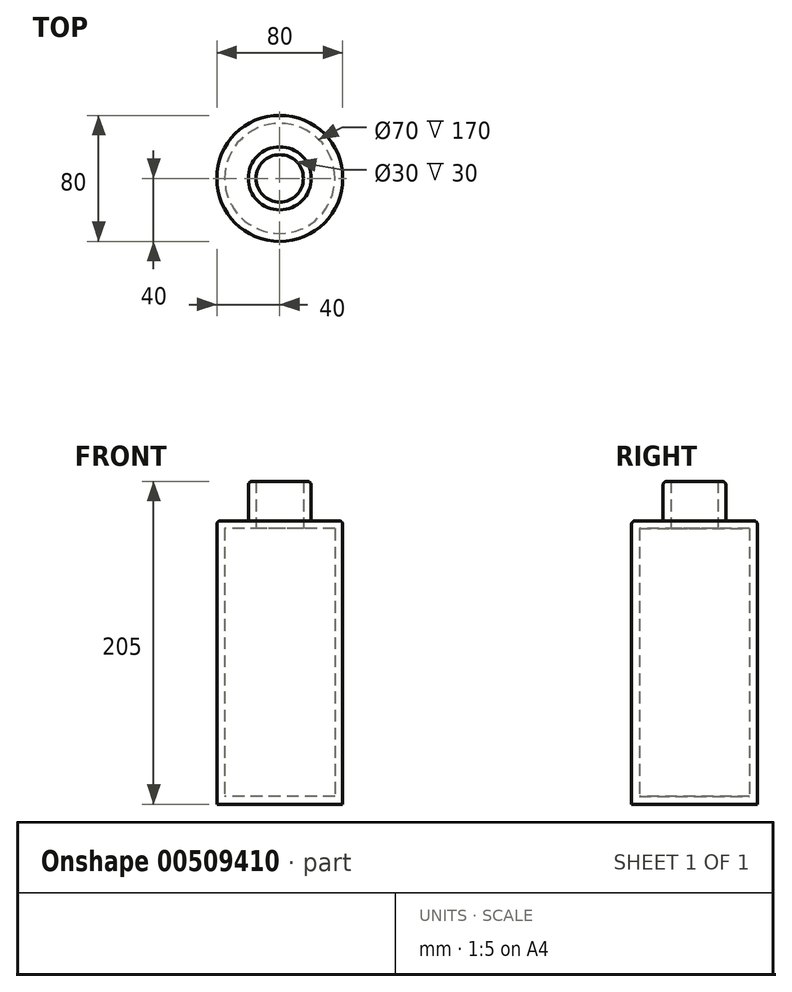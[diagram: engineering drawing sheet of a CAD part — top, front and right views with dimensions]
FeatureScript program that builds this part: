
annotation { "Feature Type Name" : "Feature", "Feature Type Description" : "" }
export const myFeature = defineFeature(function(context is Context, id is Id, definition is map)
    precondition{}
    {
        {
            var Q0;
            Q0=qCreatedBy(makeId("Top.planeOp"),FACE);
            var sketch = newSketch(context, id + "F0", { "sketchPlane" : qUnion([Q0])});
            skCircle(sketch, "E0", {"center": v(0, 0) * mm, "radius": 40 * mm});
            skSolve(sketch);
        }
        {
            var Q0;
            Q0=makeQuery(id+"F0.imprint","IMPRINT",FACE,{"disambiguationData":[TD([[makeQuery(id+"F0.imprint","IMPRINT",EDGE,{"derivedFrom":sQuery(id+"F0.wireOp",EDGE,"E0")}),1.0]])]});
            extrude(context, id + "F1", {"entities" : qUnion([Q0]), "depth" : 180 * mm});
        }
        {
            var Q0;
            Q0=makeQuery(id+"F1.opExtrude","CAP_FACE",FACE,{"disambiguationData":[OSD([sQuery(id+"F0.wireOp",EDGE,"E0")])],"isStart":false});
            var sketch = newSketch(context, id + "F2", { "sketchPlane" : qUnion([Q0])});
            skCircle(sketch, "E1", {"center": v(0, 0) * mm, "radius": 20 * mm});
            skSolve(sketch);
        }
        {
            var Q0;
            Q0=makeQuery(id+"F2.imprint","IMPRINT",FACE,{"disambiguationData":[TD([[makeQuery(id+"F2.imprint","IMPRINT",EDGE,{"derivedFrom":sQuery(id+"F2.wireOp",EDGE,"E1")}),1.0]])]});
            extrude(context, id + "F3", {"entities" : qUnion([Q0]), "operationType" : NewBodyOperationType.ADD, "depth" : 25 * mm});
        }
        {
            var Q0;
            Q0=makeQuery(id+"F3.opExtrude","CAP_EDGE",EDGE,{"disambiguationData":[OSD([sQuery(id+"F2.wireOp",EDGE,"E1")])],"isStart":false});
            var Q1;
            Q1=makeQuery(id+"F1.opExtrude","CAP_EDGE",EDGE,{"disambiguationData":[OSD([sQuery(id+"F0.wireOp",EDGE,"E0")])],"isStart":false});
            fillet(context, id + "F4", {"entities" : qUnion([Q0, Q1]), "radius" : 2.5 * mm, "tangentPropagation" : true, "allowEdgeOverflow" : false});
        }
        {
            var Q0;
            Q0=makeQuery(id+"F3.opExtrude","CAP_FACE",FACE,{"disambiguationData":[OSD([sQuery(id+"F2.wireOp",EDGE,"E1")])],"isStart":false});
            shell(context, id + "F5", {"entities" : qUnion([Q0]), "thickness" : 5 * mm});
        }
    });
